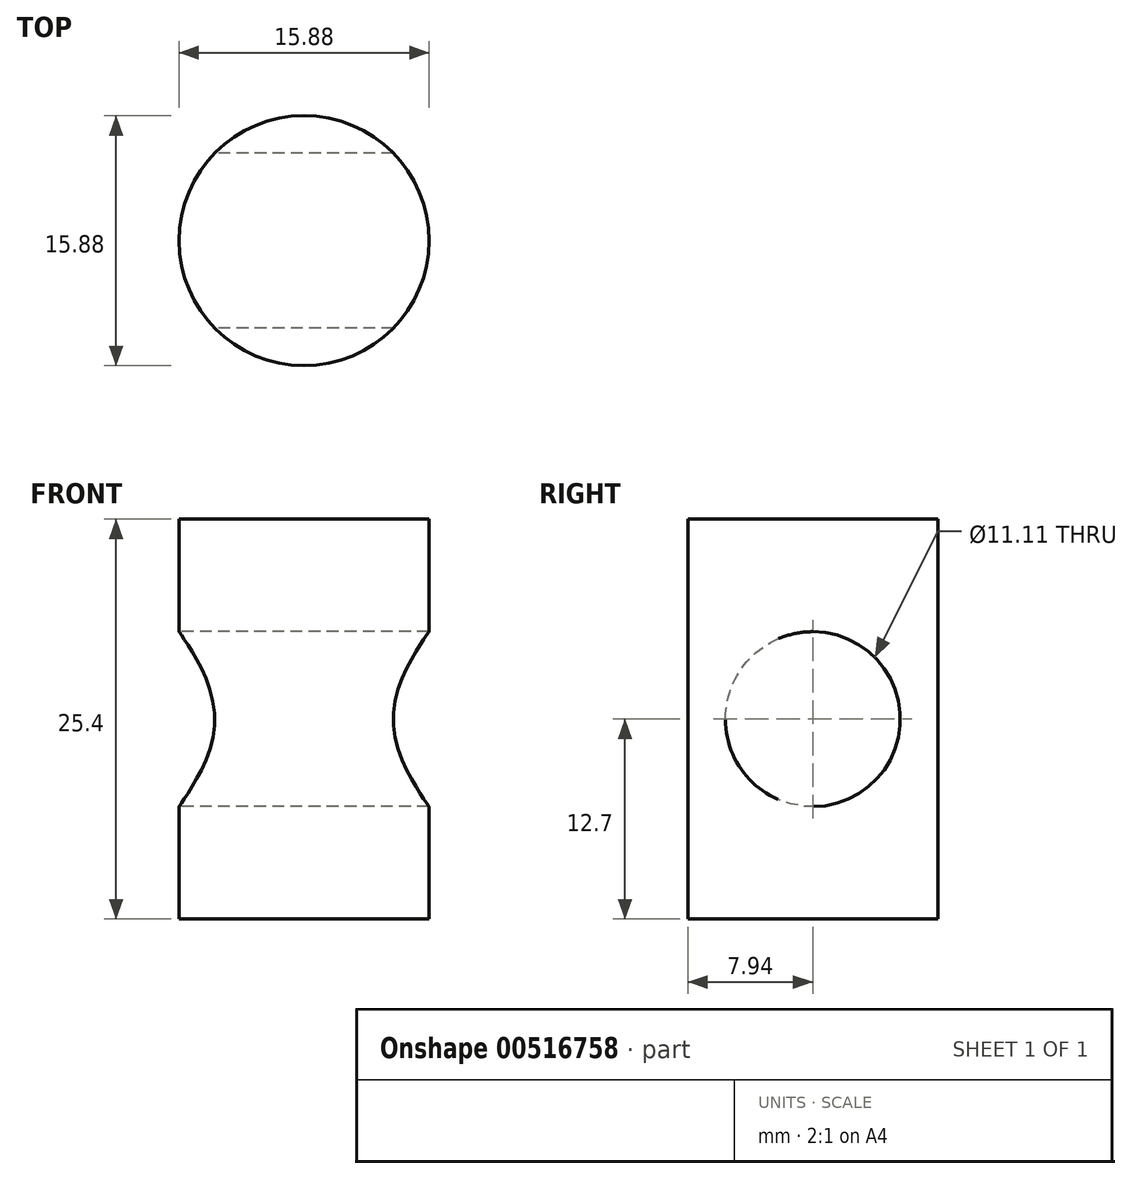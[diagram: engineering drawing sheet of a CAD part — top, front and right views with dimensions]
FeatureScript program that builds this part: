
annotation { "Feature Type Name" : "Feature", "Feature Type Description" : "" }
export const myFeature = defineFeature(function(context is Context, id is Id, definition is map)
    precondition{}
    {
        {
            var Q0;
            Q0=qCreatedBy(makeId("Top.planeOp"),FACE);
            var sketch = newSketch(context, id + "F0", { "sketchPlane" : qUnion([Q0])});
            skCircle(sketch, "E0", {"center": v(0, 0) * mm, "radius": 7.94 * mm});
            skSolve(sketch);
        }
        {
            var Q0;
            Q0=makeQuery(id+"F0.imprint","IMPRINT",FACE,{"disambiguationData":[TD([[makeQuery(id+"F0.imprint","IMPRINT",EDGE,{"derivedFrom":sQuery(id+"F0.wireOp",EDGE,"E0")}),1.0]])]});
            extrude(context, id + "F1", {"entities" : qUnion([Q0]), "depth" : 25.4 * mm, "offsetDistance" : 25.4 * mm});
        }
        {
            var Q0;
            Q0=qCreatedBy(makeId("Right.planeOp"),FACE);
            var sketch = newSketch(context, id + "F2", { "sketchPlane" : qUnion([Q0])});
            skCircle(sketch, "E1", {"center": v(0, 12.7) * mm, "radius": 5.56 * mm});
            skSolve(sketch);
        }
        {
            var Q0;
            Q0 = qSketchRegion(id + "F2", true);
            extrude(context, id + "F3", {"entities" : qUnion([Q0]), "operationType" : NewBodyOperationType.REMOVE, "endBound" : BoundingType.SYMMETRIC, "depth" : 25.4 * mm, "offsetDistance" : 25.4 * mm});
        }
    });
